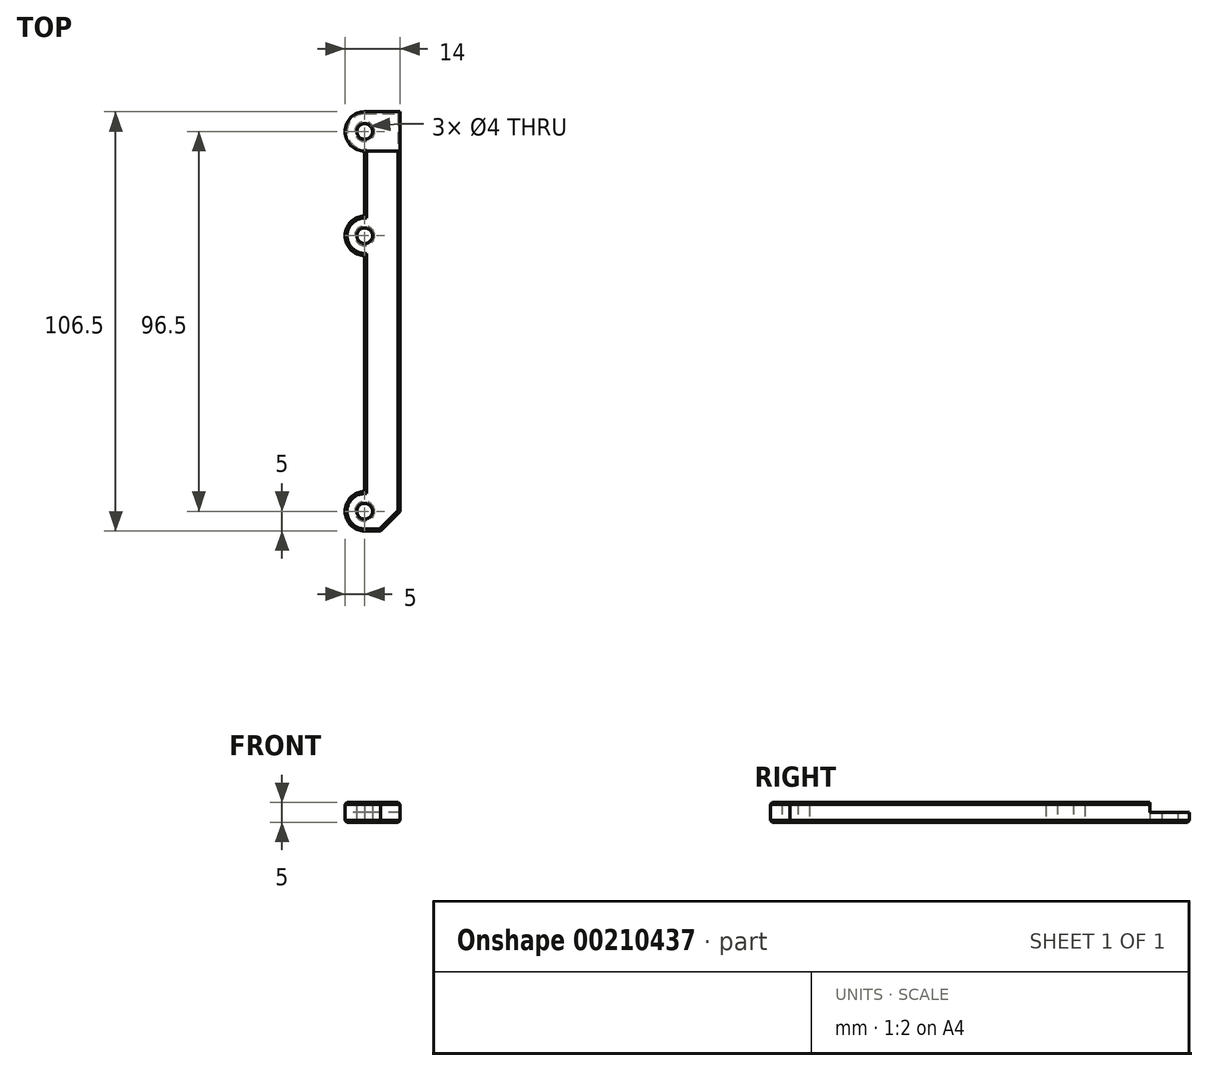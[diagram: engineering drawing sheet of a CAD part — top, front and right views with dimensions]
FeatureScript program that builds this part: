
annotation { "Feature Type Name" : "Feature", "Feature Type Description" : "" }
export const myFeature = defineFeature(function(context is Context, id is Id, definition is map)
    precondition{}
    {
        {
            var Q0;
            Q0=qCreatedBy(makeId("Top.planeOp"),FACE);
            var sketch = newSketch(context, id + "F0", { "sketchPlane" : qUnion([Q0])});
            skLineSegment(sketch, "E0.bottom", {"start": v(0, 0) * mm, "end": v(-9, 0) * mm});
            skLineSegment(sketch, "E0.top", {"start": v(0, 106.5) * mm, "end": v(-9, 106.5) * mm});
            skLineSegment(sketch, "E0.left", {"start": v(0, 0) * mm, "end": v(0, 106.5) * mm});
            skLineSegment(sketch, "E0.right", {"start": v(-9, 0) * mm, "end": v(-9, 106.5) * mm});
            skArc(sketch, "E1", {"start": v(-9, 106.5) * mm, "mid": v(-14, 101.5) * mm, "end": v(-9, 96.5) * mm});
            skArc(sketch, "E2", {"start": v(-9, 10) * mm, "mid": v(-14, 5) * mm, "end": v(-9, 0) * mm});
            skArc(sketch, "E3", {"start": v(-9, 80) * mm, "mid": v(-14, 75) * mm, "end": v(-9, 70) * mm});
            skLineSegment(sketch, "E4", {"start": v(-9, 80) * mm, "end": v(-9, 70) * mm});
            skCircle(sketch, "E5", {"center": v(-9, 101.5) * mm, "radius": 2 * mm});
            skCircle(sketch, "E6", {"center": v(-9, 75) * mm, "radius": 2 * mm});
            skCircle(sketch, "E7", {"center": v(-9, 5) * mm, "radius": 2 * mm});
            skSolve(sketch);
        }
        {
            var Q0;
            Q0 = qSketchRegion(id + "F0", true);
            extrude(context, id + "F1", {"entities" : qUnion([Q0]), "depth" : 5 * mm});
        }
        {
            var Q0;
            Q0=makeQuery(id+"F1.opExtrude","CAP_FACE",FACE,{"disambiguationData":[OSD([sQuery(id+"F0.wireOp",EDGE,"E0.bottom"),sQuery(id+"F0.wireOp",EDGE,"E0.top"),sQuery(id+"F0.wireOp",EDGE,"E0.left"),sQuery(id+"F0.wireOp",EDGE,"E0.right"),sQuery(id+"F0.wireOp",EDGE,"E1"),sQuery(id+"F0.wireOp",EDGE,"E2"),sQuery(id+"F0.wireOp",EDGE,"E3"),sQuery(id+"F0.wireOp",EDGE,"E5"),sQuery(id+"F0.wireOp",EDGE,"E6"),sQuery(id+"F0.wireOp",EDGE,"E7")])],"isStart":false});
            var sketch = newSketch(context, id + "F2", { "sketchPlane" : qUnion([Q0])});
            skLineSegment(sketch, "E8", {"start": v(-9, 96.5) * mm, "end": v(0, 96.5) * mm});
            skLineSegment(sketch, "E9", {"start": v(0, 96.5) * mm, "end": v(0, 106.5) * mm});
            skLineSegment(sketch, "E10", {"start": v(0, 106.5) * mm, "end": v(-9, 106.5) * mm});
            skArc(sketch, "E11", {"start": v(-9, 106.5) * mm, "mid": v(-14, 101.5) * mm, "end": v(-9, 96.5) * mm});
            skSolve(sketch);
        }
        {
            var Q0;
            Q0 = qSketchRegion(id + "F2", true);
            extrude(context, id + "F3", {"entities" : qUnion([Q0]), "operationType" : NewBodyOperationType.REMOVE, "oppositeDirection" : true, "depth" : 2.5 * mm});
        }
        {
            var Q0;
            Q0=makeQuery(id+"F1.opExtrude","SWEPT_EDGE",EDGE,{"disambiguationData":[OSD([sQuery(id+"F0.wireOp",EDGE,"E0.bottom"),sQuery(id+"F0.wireOp",EDGE,"E0.left")])]});
            chamfer(context, id + "F4", {"entities" : qUnion([Q0]), "width" : 5 * mm, "tangentPropagation" : true});
        }
        {
            var Q0;
            Q0=makeQuery(id+"F1.opExtrude","CAP_FACE",FACE,{"disambiguationData":[OSD([sQuery(id+"F0.wireOp",EDGE,"E0.bottom"),sQuery(id+"F0.wireOp",EDGE,"E0.top"),sQuery(id+"F0.wireOp",EDGE,"E0.left"),sQuery(id+"F0.wireOp",EDGE,"E0.right"),sQuery(id+"F0.wireOp",EDGE,"E1"),sQuery(id+"F0.wireOp",EDGE,"E2"),sQuery(id+"F0.wireOp",EDGE,"E3"),sQuery(id+"F0.wireOp",EDGE,"E5"),sQuery(id+"F0.wireOp",EDGE,"E6"),sQuery(id+"F0.wireOp",EDGE,"E7")])],"isStart":true});
            var Q1;
            Q1=makeQuery(id+"F3.boolean.opBoolean","COPY",EDGE,{"derivedFrom":makeQuery(id+"F3.opExtrude","CAP_EDGE",EDGE,{"disambiguationData":[OSD([sQuery(id+"F2.wireOp",EDGE,"E8")])],"isStart":true})});
            var Q2;
            Q2=makeQuery(id+"F1.opExtrude","CAP_EDGE",EDGE,{"disambiguationData":[OSD([sQuery(id+"F0.wireOp",EDGE,"E0.left")])],"isStart":false});
            var Q3;
            {var subQ0=sQuery(id+"F0.wireOp",EDGE,"E0.right");Q3=makeQuery(id+"F1.opExtrude","CAP_EDGE",EDGE,{"disambiguationData":[OSD([subQ0]),TDD([makeQuery(id+"F0.imprint","IMPRINT",EDGE,{"disambiguationData":[TD([[makeQuery(id+"F0.imprint","INTERSECT",VERTEX,{"derivedFrom":[subQ0,sQuery(id+"F0.wireOp",EDGE,"E1")]}),1.0]])],"derivedFrom":subQ0})])],"isStart":false});}
            var Q4;
            {var subQ0=sQuery(id+"F0.wireOp",EDGE,"E0.right");Q4=makeQuery(id+"F1.opExtrude","CAP_EDGE",EDGE,{"disambiguationData":[OSD([subQ0]),TDD([makeQuery(id+"F0.imprint","IMPRINT",EDGE,{"disambiguationData":[TD([[makeQuery(id+"F0.imprint","INTERSECT",VERTEX,{"derivedFrom":[subQ0,sQuery(id+"F0.wireOp",EDGE,"E2")]}),-1.0]])],"derivedFrom":subQ0})])],"isStart":false});}
            var Q5;
            Q5=makeQuery(id+"F1.opExtrude","CAP_EDGE",EDGE,{"disambiguationData":[OSD([sQuery(id+"F0.wireOp",EDGE,"E3")])],"isStart":false});
            var Q6;
            {var subQ0=sQuery(id+"F0.wireOp",EDGE,"E0.left");var subQ1=sQuery(id+"F0.wireOp",EDGE,"E0.bottom");Q6=makeQuery(id+"F4.opChamfer","BLEND_EDGE",EDGE,{"blendedFrom":[makeQuery(id+"F1.opExtrude","SWEPT_EDGE",EDGE,{"disambiguationData":[OSD([subQ1,subQ0])]}),makeQuery(id+"F1.opExtrude","CAP_FACE",FACE,{"disambiguationData":[OSD([subQ1,sQuery(id+"F0.wireOp",EDGE,"E0.top"),subQ0,sQuery(id+"F0.wireOp",EDGE,"E0.right"),sQuery(id+"F0.wireOp",EDGE,"E1"),sQuery(id+"F0.wireOp",EDGE,"E2"),sQuery(id+"F0.wireOp",EDGE,"E3"),sQuery(id+"F0.wireOp",EDGE,"E5"),sQuery(id+"F0.wireOp",EDGE,"E6"),sQuery(id+"F0.wireOp",EDGE,"E7")])],"isStart":false})],"blendedInto":[makeQuery(id+"F1.opExtrude","CAP_FACE",FACE,{"disambiguationData":[OSD([subQ1,sQuery(id+"F0.wireOp",EDGE,"E0.top"),subQ0,sQuery(id+"F0.wireOp",EDGE,"E0.right"),sQuery(id+"F0.wireOp",EDGE,"E1"),sQuery(id+"F0.wireOp",EDGE,"E2"),sQuery(id+"F0.wireOp",EDGE,"E3"),sQuery(id+"F0.wireOp",EDGE,"E5"),sQuery(id+"F0.wireOp",EDGE,"E6"),sQuery(id+"F0.wireOp",EDGE,"E7")])],"isStart":false})]});}
            var Q7;
            Q7=makeQuery(id+"F1.opExtrude","CAP_EDGE",EDGE,{"disambiguationData":[OSD([sQuery(id+"F0.wireOp",EDGE,"E0.bottom")])],"isStart":false});
            chamfer(context, id + "F5", {"entities" : qUnion([Q0, Q1, Q2, Q3, Q4, Q5, Q6, Q7]), "width" : .5 * mm, "tangentPropagation" : true});
        }
    });
